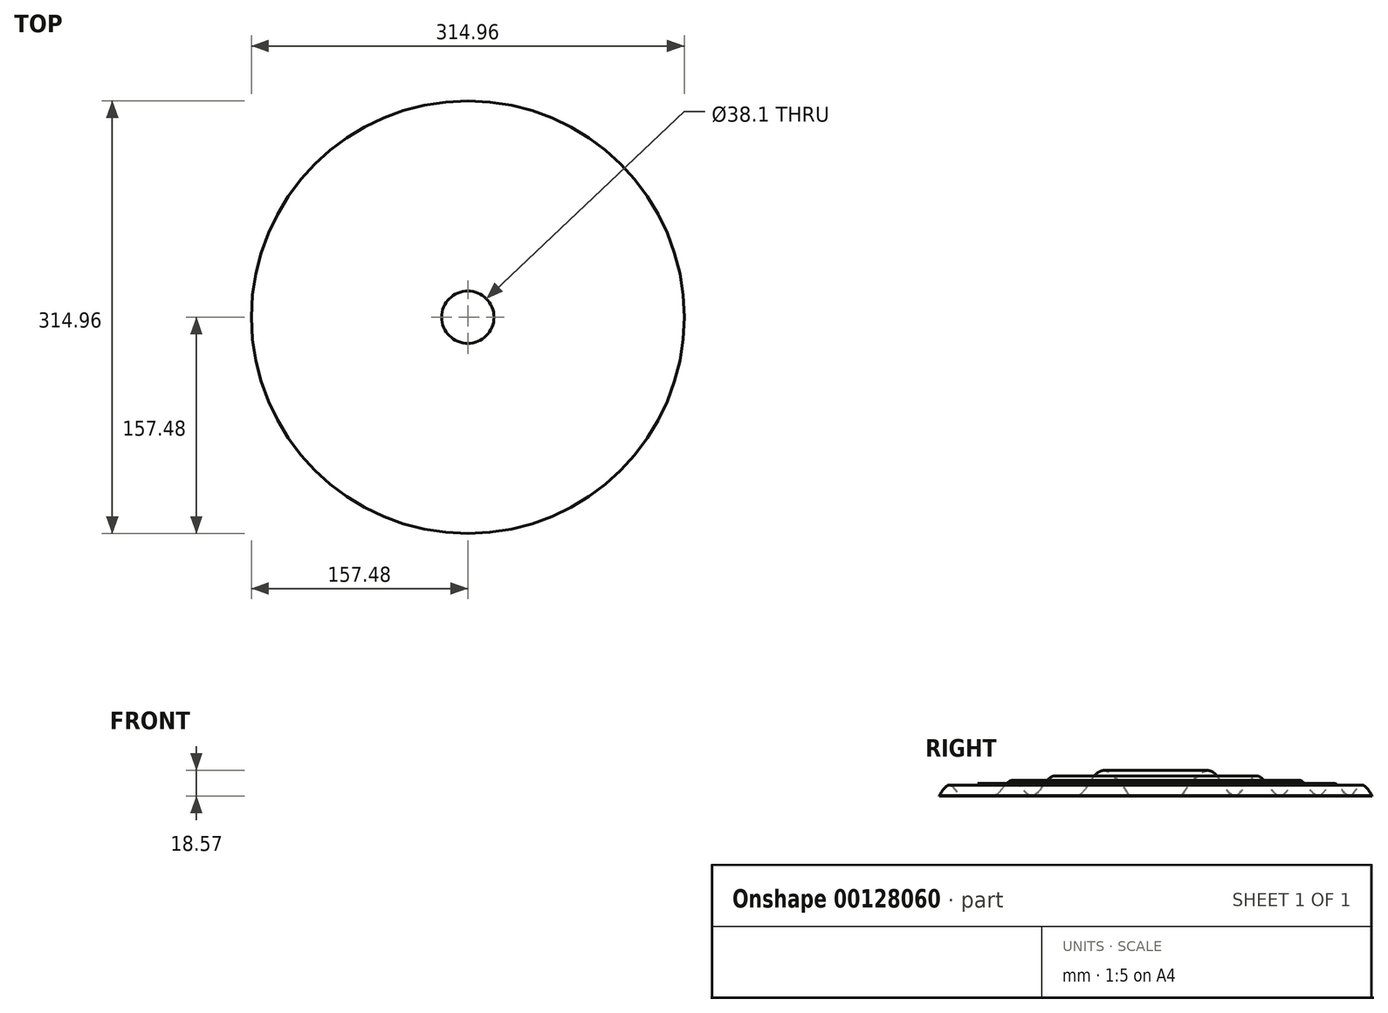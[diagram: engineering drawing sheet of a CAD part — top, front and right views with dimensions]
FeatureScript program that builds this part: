
annotation { "Feature Type Name" : "Feature", "Feature Type Description" : "" }
export const myFeature = defineFeature(function(context is Context, id is Id, definition is map)
    precondition{}
    {
        {
            var Q0;
            Q0=qCreatedBy(makeId("Front.planeOp"),FACE);
            var sketch = newSketch(context, id + "F0", { "sketchPlane" : qUnion([Q0])});
            skLineSegment(sketch, "E0", {"start": v(0, 51.98) * mm, "end": v(0, -57.5) * mm, "construction": true});
            skLineSegment(sketch, "E1", {"start": v(0, 38.1) * mm, "end": v(167.36, 7.03) * mm, "construction": true});
            skFitSpline(sketch, "E2", {"points": [v(19.05, 13.97) * mm, v(38.2, 31.01) * mm, v(57.15, 11.43) * mm, v(73.75, 24.41) * mm, v(90.17, 8.9) * mm, v(104.23, 18.75) * mm, v(118.11, 6.35) * mm, v(129.63, 14.04) * mm, v(140.97, 3.81) * mm, v(149.95, 10.27) * mm, v(157.48, 1.27) * mm], "startDerivative": vector(21.02, 49.8) * mm, "endDerivative": vector(21.53, -26.67) * mm, "construction": true});
            skFitSpline(sketch, "E3", {"points": [v(19.05, 0) * mm, v(38.2, 18.31) * mm, v(57.15, 0) * mm, v(73.75, 14.25) * mm, v(90.17, 0) * mm, v(104.23, 11.13) * mm, v(118.11, 0) * mm, v(129.63, 8.96) * mm, v(140.97, 0) * mm, v(149.95, 7.73) * mm, v(157.48, 0) * mm], "startDerivative": vector(20.65, 29.09) * mm, "endDerivative": vector(22.43, -31.08) * mm});
            skFitSpline(sketch, "E4", {"points": [v(19.05, 13.72) * mm, v(38.2, 30.76) * mm, v(57.15, 11.18) * mm, v(73.75, 24.16) * mm, v(90.17, 8.64) * mm, v(104.23, 18.5) * mm, v(118.11, 6.1) * mm, v(129.63, 13.78) * mm, v(140.97, 3.56) * mm, v(149.95, 10.01) * mm, v(157.48, 1.02) * mm], "startDerivative": vector(21.02, 34.52) * mm, "endDerivative": vector(22.25, -23.7) * mm, "construction": true});
            skLineSegment(sketch, "E5", {"start": v(19.05, 13.97) * mm, "end": v(19.05, 13.72) * mm, "construction": true});
            skLineSegment(sketch, "E6", {"start": v(157.48, 1.27) * mm, "end": v(157.48, 1.02) * mm, "construction": true});
            skFitSpline(sketch, "E7", {"points": [v(19.05, 0.25) * mm, v(38.2, 18.57) * mm, v(57.15, 0.25) * mm, v(73.75, 14.5) * mm, v(90.17, 0.25) * mm, v(104.23, 11.39) * mm, v(118.11, 0.25) * mm, v(129.63, 9.21) * mm, v(140.97, 0.25) * mm, v(149.95, 7.98) * mm, v(157.48, 0.25) * mm], "startDerivative": vector(18.41, 35.46) * mm, "endDerivative": vector(22.43, -35.52) * mm});
            skLineSegment(sketch, "E8", {"start": v(0, 0) * mm, "end": v(167.36, 0) * mm, "construction": true});
            skLineSegment(sketch, "E9", {"start": v(157.48, 0.25) * mm, "end": v(157.48, 0) * mm});
            skLineSegment(sketch, "E10", {"start": v(19.05, 0.25) * mm, "end": v(19.05, 0) * mm});
            skSolve(sketch);
        }
        {
            var Q0;
            Q0=makeQuery(id+"F0.imprint","IMPRINT",FACE,{"disambiguationData":[TD([[makeQuery(id+"F0.imprint","IMPRINT",EDGE,{"derivedFrom":sQuery(id+"F0.wireOp",EDGE,"E3")}),1.0]])]});
            var Q1;
            Q1=sQuery(id+"F0.wireOp",EDGE,"E0");
            revolve(context, id + "F1", {"entities" : qUnion([Q0]), "axis" : qUnion([Q1]), "revolveType" : RevolveType.FULL});
        }
    });
